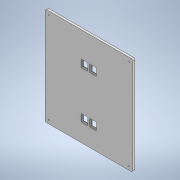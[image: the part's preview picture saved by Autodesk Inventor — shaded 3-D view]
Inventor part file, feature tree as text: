
AUTODESK INVENTOR PART (.ipt)
format: ipt  version: 2020.1 (Build 241239000, 239)  size: 158,720 bytes
history: native  units: mm
features: extrude x2, sketch x2, fillet x1
ambient origin geometry x8: Origin, YZ Plane, XZ Plane, XY Plane, X Axis, Y Axis, Z Axis, Center Point
bodies: Solid1 (feature_tree)
feature tree (5):
  extrude  "Extrusion1"  Depth=270.0mm
  fillet  "Fillet1"  Radius=10.0mm
  extrude  "Extrusion3"  Depth=6.0mm
  sketch  "Sketch1"  dims[d0=241.6mm d1=270.0mm d2=10.0mm]
  sketch  "Sketch2"  dims[d3=10.0mm d4=3.0mm d5=10.0mm d6=10.0mm d7=3.0mm d8=10.0mm d9=10.0mm d10=3.0mm d11=10.0mm d12=10.0mm d13=3.0mm d14=6.0mm d15=0.0mm d16=4.0mm d17=100.0mm d18=18.0mm d19=20.0mm d20=70.0mm d21=18.0mm d22=100.0mm d23=20.0mm d24=70.0mm d25=70.0mm d26=70.0mm d27=100.0mm d28=100.0mm d29=20.0mm d30=18.0mm d31=20.0mm d34=6.0mm d35=0.0mm]
